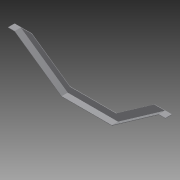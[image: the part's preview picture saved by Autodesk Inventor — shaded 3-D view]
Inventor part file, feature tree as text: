
AUTODESK INVENTOR PART (.ipt)
format: ipt  version: 2012 (Build 160160000, 160)  size: 96,768 bytes
history: native  units: in
note: dims shown in document units (in); Inventor stores cm internally (conversion verified against a paired STEP export)
features: extrude x2, sketch x1
ambient origin geometry x8: Origin, YZ Plane, XZ Plane, XY Plane, X Axis, Y Axis, Z Axis, Center Point
bodies: Solid1 (feature_tree)
feature tree (3):
  sketch  "Sketch1"  dims[d0=7.625in d1=0.9375in d2=0.9375in d3=0.9375in d4=0.9959in d5=0.9959in d6=8.704in d7=8.704in d8=5.0in d9=0.0625in d10=1.0in d11=0.0625in d12=1.0in d13=0.0625in d14=0.0625in d15=0.0in d16=1.0in d17=0.0in]
  extrude  "Extrusion1"  Depth=0.9375in
  extrude  "Extrusion2"  Depth=0.9375in
